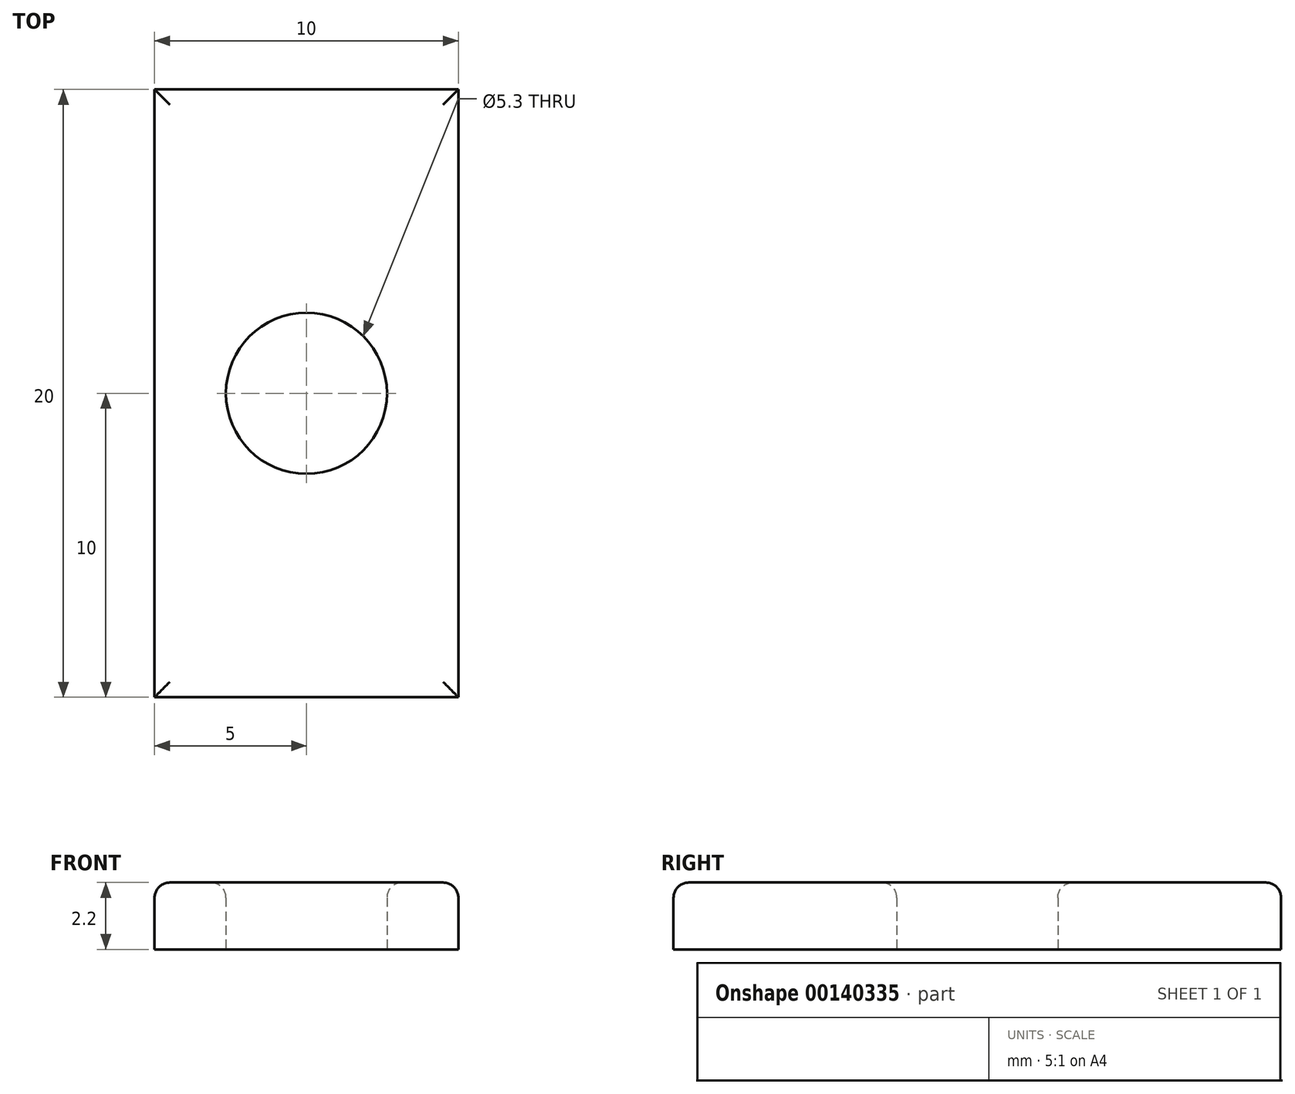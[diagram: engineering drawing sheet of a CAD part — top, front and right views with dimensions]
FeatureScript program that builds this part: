
annotation { "Feature Type Name" : "Feature", "Feature Type Description" : "" }
export const myFeature = defineFeature(function(context is Context, id is Id, definition is map)
    precondition{}
    {
        {
            var Q0;
            Q0=qCreatedBy(makeId("Top.planeOp"),FACE);
            var sketch = newSketch(context, id + "F0", { "sketchPlane" : qUnion([Q0])});
            skLineSegment(sketch, "E0.bottom", {"start": v(5, -10) * mm, "end": v(-5, -10) * mm});
            skLineSegment(sketch, "E0.top", {"start": v(5, 10) * mm, "end": v(-5, 10) * mm});
            skLineSegment(sketch, "E0.left", {"start": v(5, -10) * mm, "end": v(5, 10) * mm});
            skLineSegment(sketch, "E0.right", {"start": v(-5, -10) * mm, "end": v(-5, 10) * mm});
            skPoint(sketch, "E0.middle", {"position": v(0, 0) * mm});
            skCircle(sketch, "E1", {"center": v(0, 0) * mm, "radius": 2.65 * mm});
            skSolve(sketch);
        }
        {
            var Q0;
            Q0=makeQuery(id+"F0.imprint","IMPRINT",FACE,{"disambiguationData":[TD([[makeQuery(id+"F0.imprint","IMPRINT",EDGE,{"derivedFrom":sQuery(id+"F0.wireOp",EDGE,"E0.bottom")}),-1.0]])]});
            extrude(context, id + "F1", {"entities" : qUnion([Q0]), "depth" : 2.2 * mm});
        }
        {
            var Q0;
            Q0=makeQuery(id+"F1.opExtrude","CAP_EDGE",EDGE,{"disambiguationData":[OSD([sQuery(id+"F0.wireOp",EDGE,"E1")])],"isStart":false});
            var Q1;
            Q1=makeQuery(id+"F1.opExtrude","CAP_EDGE",EDGE,{"disambiguationData":[OSD([sQuery(id+"F0.wireOp",EDGE,"E0.left")])],"isStart":false});
            var Q2;
            Q2=makeQuery(id+"F1.opExtrude","CAP_EDGE",EDGE,{"disambiguationData":[OSD([sQuery(id+"F0.wireOp",EDGE,"E0.top")])],"isStart":false});
            var Q3;
            Q3=makeQuery(id+"F1.opExtrude","CAP_FACE",FACE,{"disambiguationData":[OSD([sQuery(id+"F0.wireOp",EDGE,"E0.bottom"),sQuery(id+"F0.wireOp",EDGE,"E0.top"),sQuery(id+"F0.wireOp",EDGE,"E0.left"),sQuery(id+"F0.wireOp",EDGE,"E0.right"),sQuery(id+"F0.wireOp",EDGE,"E1")])],"isStart":false});
            fillet(context, id + "F2", {"entities" : qUnion([Q0, Q1, Q2, Q3]), "radius" : 0.5 * mm, "tangentPropagation" : true, "allowEdgeOverflow" : false});
        }
    });
